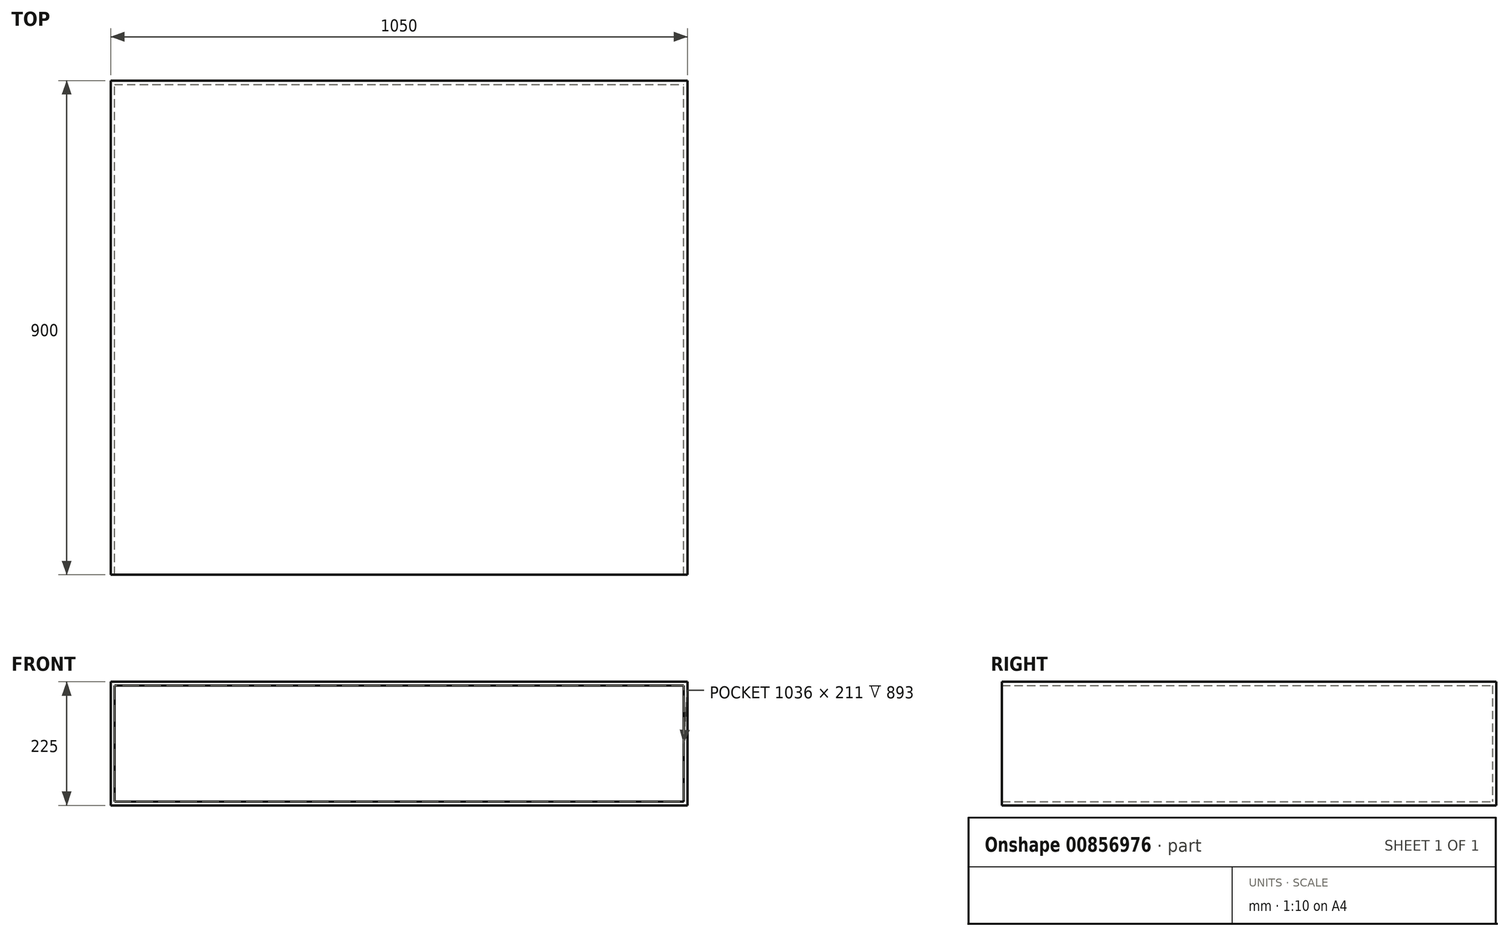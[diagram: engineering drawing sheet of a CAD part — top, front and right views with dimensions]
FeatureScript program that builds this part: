
annotation { "Feature Type Name" : "Feature", "Feature Type Description" : "" }
export const myFeature = defineFeature(function(context is Context, id is Id, definition is map)
    precondition{}
    {
        {
            var Q0;
            Q0=qCreatedBy(makeId("Right.planeOp"),FACE);
            var sketch = newSketch(context, id + "F0", { "sketchPlane" : qUnion([Q0])});
            skLineSegment(sketch, "E0.bottom", {"start": v(0, 0) * mm, "end": v(900, 0) * mm});
            skLineSegment(sketch, "E0.top", {"start": v(0, -225) * mm, "end": v(900, -225) * mm});
            skLineSegment(sketch, "E0.left", {"start": v(0, 0) * mm, "end": v(0, -225) * mm});
            skLineSegment(sketch, "E0.right", {"start": v(900, 0) * mm, "end": v(900, -225) * mm});
            skSolve(sketch);
        }
        {
            var Q0;
            Q0=makeQuery(id+"F0.imprint","IMPRINT",FACE,{"disambiguationData":[TD([[makeQuery(id+"F0.imprint","IMPRINT",EDGE,{"derivedFrom":sQuery(id+"F0.wireOp",EDGE,"E0.bottom")}),-1.0]])]});
            extrude(context, id + "F1", {"entities" : qUnion([Q0]), "oppositeDirection" : true, "depth" : 1050 * mm, "offsetDistance" : 25 * mm});
        }
        {
            var Q0;
            Q0=makeQuery(id+"F1.opExtrude","SWEPT_FACE",FACE,{"disambiguationData":[OSD([sQuery(id+"F0.wireOp",EDGE,"E0.left")])]});
            shell(context, id + "F2", {"entities" : qUnion([Q0]), "thickness" : 7 * mm});
        }
        {
            var Q0;
            Q0=makeQuery(id+"F1.opExtrude","SWEPT_FACE",FACE,{"disambiguationData":[OSD([sQuery(id+"F0.wireOp",EDGE,"E0.bottom")])]});
            var sketch = newSketch(context, id + "F3", { "sketchPlane" : qUnion([Q0])});
            skLineSegment(sketch, "E1", {"start": v(-525, 900) * mm, "end": v(-525, 880) * mm, "construction": true});
            skSolve(sketch);
        }
    });
